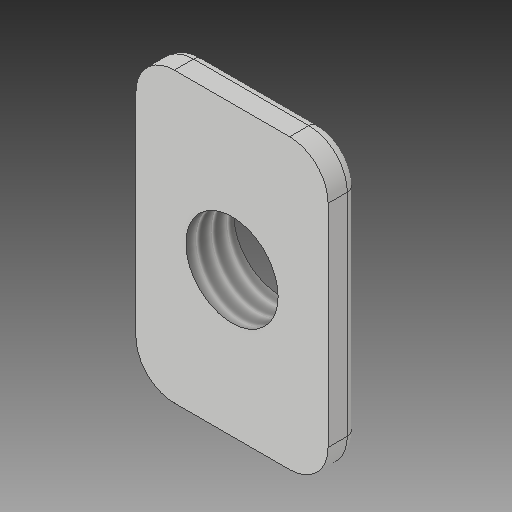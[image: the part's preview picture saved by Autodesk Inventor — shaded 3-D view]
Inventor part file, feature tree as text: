
AUTODESK INVENTOR PART (.ipt)
format: ipt  version: 2018 (Build 220112000, 112)  size: 147,456 bytes
history: native  units: mm
features: other x3, sketch x2
ambient origin geometry x8: Origin, YZ Plane, XZ Plane, XY Plane, X Axis, Y Axis, Z Axis, Center Point
bodies: Solid1 (feature_tree)
feature tree (5):
  other  "M5 Tee Nut_MIR_MIR_MIR_MIR.ipt"
  other  "Solid1::M5 Tee Nut_MIR_MIR_MIR_MIR.ipt"
  other  "TaggingFeature1"
  sketch  "Sketch1"  dims[d0=10.0mm]
  sketch  "Sketch2"
